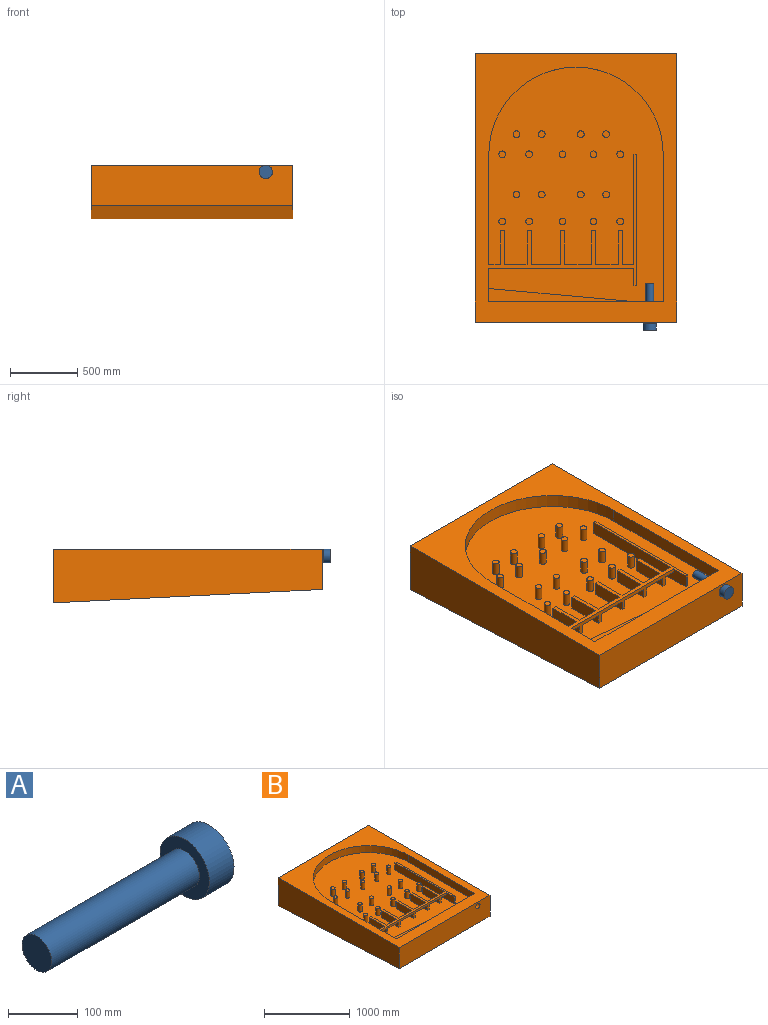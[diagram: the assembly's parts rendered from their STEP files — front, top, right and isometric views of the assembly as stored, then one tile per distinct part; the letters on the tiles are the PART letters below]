
ASSEMBLY  parts=2 mates=1
PART A: 5 faces, bbox 350x100x100 mm
  f0: cylinder r=30mm len=300mm, axis (-1,0,0), area 56548.7mm2, adj f1,f4
  f1: plane 60x60mm, normal (-1,0,0), area 2827.4mm2, adj f0
  f2: cylinder r=50mm len=100mm, axis (-1,0,0), area 15708mm2, adj f3,f4
  f3: plane 100x100mm, normal (1,0,0), area 7854mm2, adj f2
  f4: plane 100x100mm, normal (-1,0,0), area 5026.5mm2, adj f0,f2
PART B: 82 faces, bbox 1500x2000x400 mm
  f0: plane 85x30mm, normal (0,1,0), area 2550mm2, adj f7,f16,f60,f80
  f1: plane 1080x100mm, normal (0,-1,0), area 42900mm2, adj f7,f8,f16,f23,f60,f61,f63,f64
  f2: plane 85x30mm, normal (0,1,0), area 2550mm2, adj f16,f23,f61,f79
  f3: plane 170x30mm, normal (0,1,0), area 5100mm2, adj f16,f63,f64,f78
  f4: plane 200x30mm, normal (0,1,0), area 6000mm2, adj f16,f66,f67,f77
  f5: plane 220x30mm, normal (0,1,0), area 6600mm2, adj f16,f69,f70,f76
  f6: plane 170x30mm, normal (0,1,0), area 5100mm2, adj f16,f72,f73,f75
  f7: plane 1100x100mm, normal (1,0,0), area 104100mm2, adj f0,f1,f8,f13,f14,f16,f17,f18
  f8: plane 1750x1300mm, normal (0,0,1), area 1941718.5mm2, adj f1,f7,f13,f14,f15,f17,f20,f21
  f9: plane 2000x400mm, normal (-1,0,0), area 700000mm2, adj f10,f12,f16,f81
  f10: plane 1500x300mm, normal (0,-1,0), area 446151.5mm2, adj f9,f11,f16,f19,f81
  f11: plane 2000x400mm, normal (1,0,0), area 700000mm2, adj f10,f12,f16,f81
  f12: plane 1500x400mm, normal (0,1,0), area 600000mm2, adj f9,f11,f16,f81
  f13: plane 1300x100mm, normal (0,1,0), area 71151.5mm2, adj f7,f8,f15,f16,f17,f18,f19
  f14: cylinder r=650mm len=1300mm, axis (0,0,-1), area 204203.5mm2, adj f7,f8,f15,f16
  f15: plane 1100x100mm, normal (-1,0,0), area 110000mm2, adj f8,f13,f14,f16
  f16: plane 2000x1500mm, normal (0,0,1), area 995838.6mm2, adj f0,f1,f2,f3,f4,f5,f6,f7
  f17: plane 1100x100mm, normal (0.09,1,0), area 55226.8mm2, adj f7,f8,f13,f18
  f18: plane 1100x100mm, normal (0,0,1), area 55000mm2, adj f7,f13,f17
  f19: cylinder r=35mm len=150mm, axis (0,-1,0), area 32986.7mm2, adj f10,f13
  f20: plane 100x20mm, normal (0,-1,0), area 2000mm2, adj f8,f16,f21,f23
  f21: plane 980x100mm, normal (1,0,0), area 98000mm2, adj f8,f16,f20,f22
  f22: plane 100x20mm, normal (0,1,0), area 2000mm2, adj f8,f16,f21,f23
  f23: plane 980x100mm, normal (-1,0,0), area 97100mm2, adj f1,f2,f8,f16,f20,f22,f79
  f24: cylinder r=25mm len=100mm, axis (0,0,-1), area 15708mm2, adj f8,f25
  f25: plane 50x50mm, normal (0,0,1), area 1963.5mm2, adj f24
  f26: cylinder r=25mm len=100mm, axis (0,0,-1), area 15708mm2, adj f8,f27
  f27: plane 50x50mm, normal (0,0,1), area 1963.5mm2, adj f26
  f28: cylinder r=25mm len=100mm, axis (0,0,-1), area 15708mm2, adj f8,f29
  f29: plane 50x50mm, normal (0,0,1), area 1963.5mm2, adj f28
  f30: cylinder r=25mm len=100mm, axis (0,0,-1), area 15708mm2, adj f8,f31
  f31: plane 50x50mm, normal (0,0,1), area 1963.5mm2, adj f30
  f32: cylinder r=25mm len=100mm, axis (0,0,-1), area 15708mm2, adj f8,f33
  f33: plane 50x50mm, normal (0,0,1), area 1963.5mm2, adj f32
  f34: cylinder r=25mm len=100mm, axis (0,0,-1), area 15708mm2, adj f8,f35
  f35: plane 50x50mm, normal (0,0,1), area 1963.5mm2, adj f34
  f36: cylinder r=25mm len=100mm, axis (0,0,-1), area 15708mm2, adj f8,f37
  f37: plane 50x50mm, normal (0,0,1), area 1963.5mm2, adj f36
  f38: cylinder r=25mm len=100mm, axis (0,0,-1), area 15708mm2, adj f8,f39
  f39: plane 50x50mm, normal (0,0,1), area 1963.5mm2, adj f38
  f40: cylinder r=25mm len=100mm, axis (0,0,-1), area 15708mm2, adj f8,f41
  f41: plane 50x50mm, normal (0,0,1), area 1963.5mm2, adj f40
  f42: cylinder r=25mm len=100mm, axis (0,0,-1), area 15708mm2, adj f8,f43
  f43: plane 50x50mm, normal (0,0,1), area 1963.5mm2, adj f42
  f44: cylinder r=25mm len=100mm, axis (0,0,-1), area 15708mm2, adj f8,f45
  f45: plane 50x50mm, normal (0,0,1), area 1963.5mm2, adj f44
  f46: cylinder r=25mm len=100mm, axis (0,0,-1), area 15708mm2, adj f8,f47
  f47: plane 50x50mm, normal (0,0,1), area 1963.5mm2, adj f46
  f48: cylinder r=25mm len=100mm, axis (0,0,-1), area 15708mm2, adj f8,f49
  f49: plane 50x50mm, normal (0,0,1), area 1963.5mm2, adj f48
  f50: cylinder r=25mm len=100mm, axis (0,0,-1), area 15708mm2, adj f8,f51
  f51: plane 50x50mm, normal (0,0,1), area 1963.5mm2, adj f50
  f52: cylinder r=25mm len=100mm, axis (0,0,-1), area 15708mm2, adj f8,f53
  f53: plane 50x50mm, normal (0,0,1), area 1963.5mm2, adj f52
  f54: cylinder r=25mm len=100mm, axis (0,0,-1), area 15708mm2, adj f8,f55
  f55: plane 50x50mm, normal (0,0,1), area 1963.5mm2, adj f54
  f56: cylinder r=25mm len=100mm, axis (0,0,-1), area 15708mm2, adj f8,f57
  f57: plane 50x50mm, normal (0,0,1), area 1963.5mm2, adj f56
  f58: cylinder r=25mm len=100mm, axis (0,0,-1), area 15708mm2, adj f8,f59
  f59: plane 50x50mm, normal (0,0,1), area 1963.5mm2, adj f58
  f60: plane 280x100mm, normal (-1,0,0), area 27100mm2, adj f0,f1,f8,f16,f74,f80
  f61: plane 280x100mm, normal (1,0,0), area 27100mm2, adj f1,f2,f8,f16,f62,f79
  f62: plane 100x30mm, normal (0,1,0), area 3000mm2, adj f8,f16,f61,f63
  f63: plane 280x100mm, normal (-1,0,0), area 27100mm2, adj f1,f3,f8,f16,f62,f78
  f64: plane 280x100mm, normal (1,0,0), area 27100mm2, adj f1,f3,f8,f16,f65,f78
  f65: plane 100x30mm, normal (0,1,0), area 3000mm2, adj f8,f16,f64,f66
  f66: plane 280x100mm, normal (-1,0,0), area 27100mm2, adj f1,f4,f8,f16,f65,f77
  f67: plane 280x100mm, normal (1,0,0), area 27100mm2, adj f1,f4,f8,f16,f68,f77
  f68: plane 100x30mm, normal (0,1,0), area 3000mm2, adj f8,f16,f67,f69
  f69: plane 280x100mm, normal (-1,0,0), area 27100mm2, adj f1,f5,f8,f16,f68,f76
  f70: plane 280x100mm, normal (1,0,0), area 27100mm2, adj f1,f5,f8,f16,f71,f76
  f71: plane 100x30mm, normal (0,1,0), area 3000mm2, adj f8,f16,f70,f72
  f72: plane 280x100mm, normal (-1,0,0), area 27100mm2, adj f1,f6,f8,f16,f71,f75
  f73: plane 280x100mm, normal (1,0,0), area 27100mm2, adj f1,f6,f8,f16,f74,f75
  f74: plane 100x30mm, normal (0,1,0), area 3000mm2, adj f8,f16,f60,f73
  f75: plane 170x30mm, normal (0,0,-1), area 5100mm2, adj f1,f6,f72,f73
  f76: plane 220x30mm, normal (0,0,-1), area 6600mm2, adj f1,f5,f69,f70
  f77: plane 200x30mm, normal (0,0,-1), area 6000mm2, adj f1,f4,f66,f67
  f78: plane 170x30mm, normal (0,0,-1), area 5100mm2, adj f1,f3,f63,f64
  f79: plane 85x30mm, normal (0,0,-1), area 2550mm2, adj f1,f2,f23,f61
  f80: plane 85x30mm, normal (0,0,-1), area 2550mm2, adj f0,f1,f7,f60
  f81: plane 2000x1500mm, normal (0,-0.05,-1), area 3003747.7mm2, adj f9,f10,f11,f12
PLACE A rot(axis=(0,0,-1),90deg) t=(680.25,-711.33,320.26)mm
PLACE B t=(130.25,0,70.26)mm
MATE slider A.f0 <-> B.f19  axis (0,1,0) through (680.25,-711.33,320.26)mm
